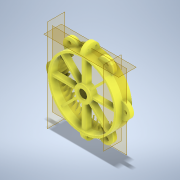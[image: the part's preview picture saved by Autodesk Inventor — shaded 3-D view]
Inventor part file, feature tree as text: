
AUTODESK INVENTOR PART (.ipt)
format: ipt  version: 2021.2 (Build 252289000, 289)  size: 883,712 bytes
history: native  units: in
note: dims shown in document units (in); Inventor stores cm internally (conversion verified against a paired STEP export)
features: extrude x11, sketch x11, plane x4, pattern_circular x3, fillet x2
ambient origin geometry x8: Origin, YZ Plane, XZ Plane, XY Plane, X Axis, Y Axis, Z Axis, Center Point
bodies: Solid1 (feature_tree)
feature tree (31):
  extrude  "Extrusion1"  Depth=4.25in
  plane  "Work Plane1"
  plane  "Work Plane2"
  extrude  "Extrusion3"  Depth=1.4in
  fillet  "Fillet1"  Radius=2.125in
  extrude  "Extrusion4"  TaperAngle=0.0deg  [1 undecoded]
  pattern_circular  "Circular Pattern2"  Count=2 Angle=360.0deg
  plane  "Work Plane3"
  extrude  "Extrusion5"  Depth=1.0in
  extrude  "Extrusion6"  Depth=0.25in
  fillet  "Fillet2"  [1 undecoded]
  extrude  "Extrusion7"  Depth=0.0787in TaperAngle=0.0deg
  pattern_circular  "Circular Pattern3"  [2 undecoded]
  extrude  "Extrusion14"  Depth=0.25in
  pattern_circular  "Circular Pattern9"  [2 undecoded]
  extrude  "Extrusion15"  Depth=0.0787in TaperAngle=0.0deg
  plane  "Work Plane4"
  extrude  "Extrusion16"  Depth=0.0787in TaperAngle=360.0deg
  extrude  "Extrusion17"  Depth=0.25in
  extrude  "Extrusion18"  Depth=0.125in
  sketch  "Sketch1"  dims[d0=4.0in d1=4.25in]
  sketch  "Sketch3"  dims[d2=1.0in d3=0.0in d4=1.4in d10=2.125in]
  sketch  "Sketch4"  dims[d11=0.25in d12=0.0in]
  sketch  "Sketch5"  dims[d13=0.5in d14=0.0in]
  sketch  "Sketch6"  dims[d15=0.5in]
  sketch  "Sketch7"  dims[d16=0.125in]
  sketch  "Sketch8"  dims[d17=0.2in]
  sketch  "Sketch11"  dims[d18=0.5in d19=0.0in d20=0.7874in d21=360.0deg]
  sketch  "Sketch12"  dims[d23=-2.125in d24=1.0in]
  sketch  "Sketch13"  dims[d25=0.25in d26=0.5in d27=0.0in]
  sketch  "Sketch14"  dims[d28=0.1in d29=0.0in d30=0.5in d31=0.0in d32=0.5in d33=0.25in d34=0.2in d35=0.5in d36=0.0in d37=2.3622in d38=360.0deg d40=0.25in d41=0.125in d42=0.25in d43=0.2in d49=0.5in d50=0.0312in d79=0.65in d80=0.0in d81=18.8976in d82=360.0deg d84=3.4625in d85=0.0in d86=0.0777in d87=-0.4688in d88=4.0in d89=90.0deg d90=0.25in d91=4.0in d92=0.0in d93=0.125in d94=4.0in d95=45.0deg d96=0.125in d97=4.0in d98=135.0deg d99=0.125in d100=1.0236in d101=0.8661in d102=0.3543in d103=0.0in d104=0.5512in d105=0.0787in d106=0.0in d107=0.0787in d108=0.0in]
note: 6 required parameter values undecoded (feature->parameter linkage not recoverable at this tier; creation-order binding heuristic only, values carry confidence <= 0.55)
